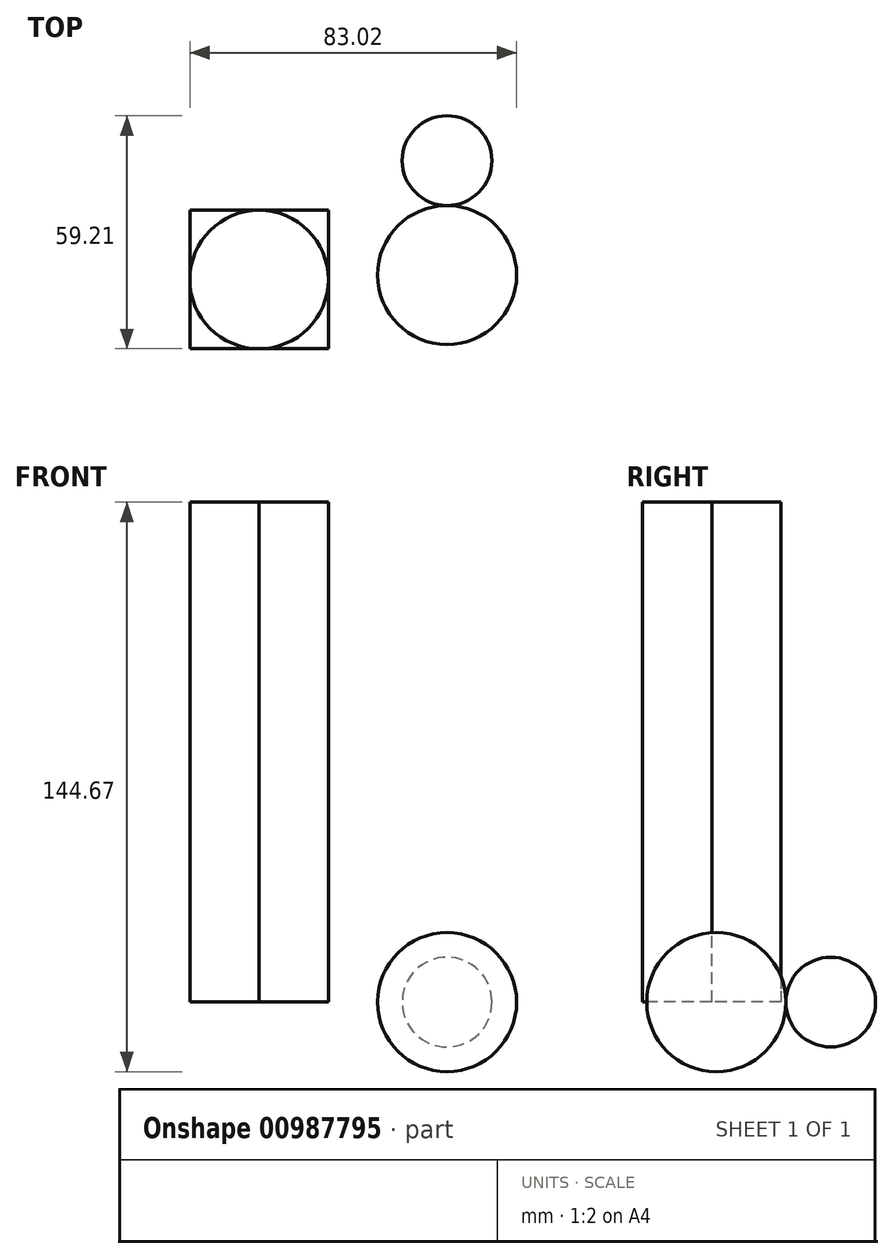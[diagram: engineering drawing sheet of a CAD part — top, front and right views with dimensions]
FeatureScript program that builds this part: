
annotation { "Feature Type Name" : "Feature", "Feature Type Description" : "" }
export const myFeature = defineFeature(function(context is Context, id is Id, definition is map)
    precondition{}
    {
        {
            var Q0;
            Q0=qCreatedBy(makeId("Top.planeOp"),FACE);
            var sketch = newSketch(context, id + "F0", { "sketchPlane" : qUnion([Q0])});
            skCircle(sketch, "E0", {"center": v(0, 0) * mm, "radius": 25.4 * mm, "construction": true});
            skCircle(sketch, "E1", {"center": v(0, 43.07) * mm, "radius": 17.67 * mm, "construction": true});
            skCircle(sketch, "E2", {"center": v(0, 72.14) * mm, "radius": 11.4 * mm, "construction": true});
            skLineSegment(sketch, "E3", {"start": v(0, -42.75) * mm, "end": v(0, 93.8) * mm, "construction": true});
            skArc(sketch, "E4", {"start": v(0, 83.54) * mm, "mid": v(-11.4, 72.14) * mm, "end": v(0, 60.73) * mm});
            skArc(sketch, "E5", {"start": v(0, 60.73) * mm, "mid": v(-17.67, 43.07) * mm, "end": v(0, 25.4) * mm});
            skArc(sketch, "E6", {"start": v(0, -25.4) * mm, "mid": v(-25.4, 0) * mm, "end": v(0, 25.4) * mm});
            skLineSegment(sketch, "E7", {"start": v(0, 83.54) * mm, "end": v(0, -25.4) * mm});
            skSolve(sketch);
        }
        {
            var Q0;
            {var subQ0=sQuery(id+"F0.wireOp",EDGE,"E4");Q0=makeQuery(id+"F0.imprint","IMPRINT",FACE,{"disambiguationData":[TD([[makeQuery(id+"F0.imprint","IMPRINT",EDGE,{"derivedFrom":subQ0}),1.0]])]});}
            var Q1;
            {var subQ0=sQuery(id+"F0.wireOp",EDGE,"E5");Q1=makeQuery(id+"F0.imprint","IMPRINT",FACE,{"disambiguationData":[TD([[makeQuery(id+"F0.imprint","IMPRINT",EDGE,{"derivedFrom":subQ0}),1.0]])]});}
            var Q2;
            {var subQ0=sQuery(id+"F0.wireOp",EDGE,"E6");Q2=makeQuery(id+"F0.imprint","IMPRINT",FACE,{"disambiguationData":[TD([[makeQuery(id+"F0.imprint","IMPRINT",EDGE,{"derivedFrom":subQ0}),-1.0]])]});}
            var Q3;
            Q3=sQuery(id+"F0.wireOp",EDGE,"E3");
            revolve(context, id + "F1", {"surfaceOperationType" : NewSurfaceOperationType.NEW, "entities" : qUnion([Q0, Q1, Q2]), "axis" : qUnion([Q3]), "revolveType" : RevolveType.FULL});
        }
        {
            var Q0;
            Q0=qCreatedBy(makeId("Top.planeOp"),FACE);
            var sketch = newSketch(context, id + "F2", { "sketchPlane" : qUnion([Q0])});
            skLineSegment(sketch, "E8.bottom", {"start": v(-65.35, 59.53) * mm, "end": v(-30.15, 59.53) * mm});
            skLineSegment(sketch, "E8.top", {"start": v(-65.35, 24.33) * mm, "end": v(-30.15, 24.33) * mm});
            skLineSegment(sketch, "E8.left", {"start": v(-65.35, 59.53) * mm, "end": v(-65.35, 24.33) * mm});
            skLineSegment(sketch, "E8.right", {"start": v(-30.15, 59.53) * mm, "end": v(-30.15, 24.33) * mm});
            skSolve(sketch);
        }
        {
            var Q0;
            Q0=makeQuery(id+"F2.imprint","IMPRINT",FACE,{"disambiguationData":[TD([[makeQuery(id+"F2.imprint","IMPRINT",EDGE,{"derivedFrom":sQuery(id+"F2.wireOp",EDGE,"E8.bottom")}),-1.0]])]});
            extrude(context, id + "F3", {"entities" : qUnion([Q0]), "depth" : 127 * mm, "offsetDistance" : 25.4 * mm});
        }
        {
            var Q0;
            Q0=makeQuery(id+"F3.opExtrude","CAP_FACE",FACE,{"disambiguationData":[OSD([sQuery(id+"F2.wireOp",EDGE,"E8.bottom"),sQuery(id+"F2.wireOp",EDGE,"E8.top"),sQuery(id+"F2.wireOp",EDGE,"E8.left"),sQuery(id+"F2.wireOp",EDGE,"E8.right")])],"isStart":false});
            var sketch = newSketch(context, id + "F4", { "sketchPlane" : qUnion([Q0])});
            skCircle(sketch, "E9", {"center": v(-47.75, 41.93) * mm, "radius": 17.6 * mm});
            skLineSegment(sketch, "E10", {"start": v(-30.15, 41.93) * mm, "end": v(-65.35, 41.93) * mm, "construction": true});
            skLineSegment(sketch, "E11", {"start": v(-47.75, 59.53) * mm, "end": v(-47.75, 24.33) * mm, "construction": true});
            skSolve(sketch);
        }
        {
            var Q0;
            {var subQ0=sQuery(id+"F4.wireOp",EDGE,"E9");var subQ1=makeQuery(id+"F4.imprint","INTERSECT",VERTEX,{"derivedFrom":[makeQuery(id+"F3.opExtrude","CAP_EDGE",EDGE,{"disambiguationData":[OSD([sQuery(id+"F2.wireOp",EDGE,"E8.bottom")])],"isStart":false}),subQ0]});Q0=makeQuery(id+"F4.imprint","IMPRINT",FACE,{"disambiguationData":[TD([[makeQuery(id+"F4.imprint","IMPRINT",EDGE,{"disambiguationData":[TD([[subQ1,1.0]])],"derivedFrom":subQ0}),1.0]])]});}
            extrude(context, id + "F5", {"entities" : qUnion([Q0]), "operationType" : NewBodyOperationType.REMOVE, "endBound" : BoundingType.THROUGH_ALL, "oppositeDirection" : true, "depth" : 25.4 * mm, "offsetDistance" : 25.4 * mm});
        }
    });
